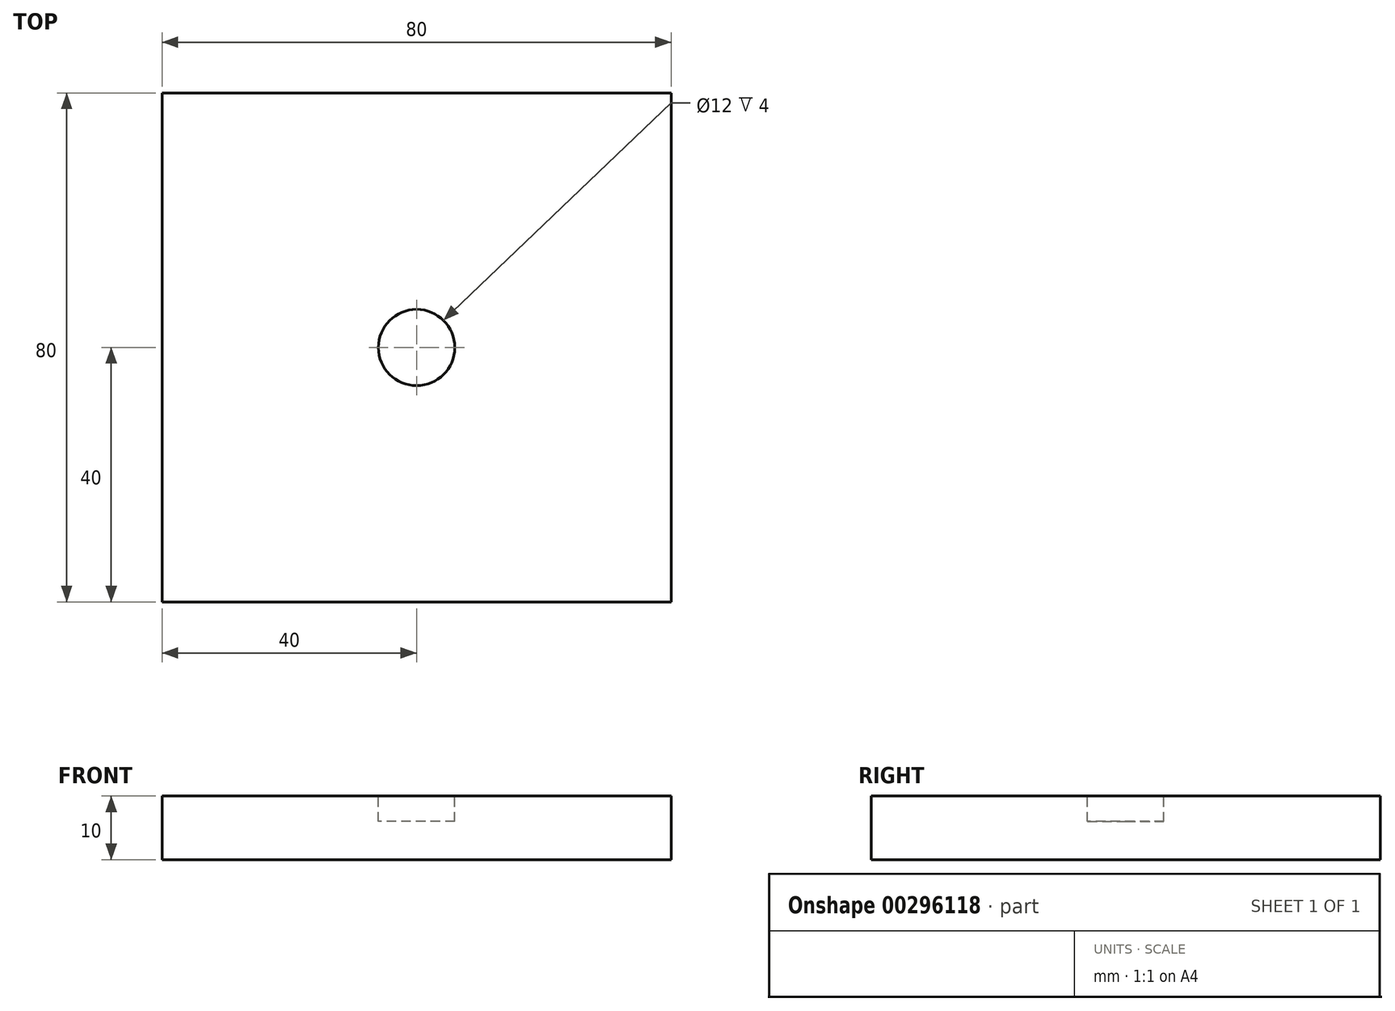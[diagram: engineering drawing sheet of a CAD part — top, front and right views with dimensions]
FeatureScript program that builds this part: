
annotation { "Feature Type Name" : "Feature", "Feature Type Description" : "" }
export const myFeature = defineFeature(function(context is Context, id is Id, definition is map)
    precondition{}
    {
        {
            var Q0;
            Q0=qCreatedBy(makeId("Top.planeOp"),FACE);
            var sketch = newSketch(context, id + "F0", { "sketchPlane" : qUnion([Q0])});
            skLineSegment(sketch, "E0.bottom", {"start": v(40, 40) * mm, "end": v(-40, 40) * mm});
            skLineSegment(sketch, "E0.top", {"start": v(40, -40) * mm, "end": v(-40, -40) * mm});
            skLineSegment(sketch, "E0.left", {"start": v(40, 40) * mm, "end": v(40, -40) * mm});
            skLineSegment(sketch, "E0.right", {"start": v(-40, 40) * mm, "end": v(-40, -40) * mm});
            skPoint(sketch, "E0.middle", {"position": v(0, 0) * mm});
            skSolve(sketch);
        }
        {
            var Q0;
            Q0 = qSketchRegion(id + "F0", true);
            extrude(context, id + "F1", {"entities" : qUnion([Q0]), "oppositeDirection" : true, "depth" : 10 * mm, "offsetDistance" : 25 * mm});
        }
        {
            var Q0;
            Q0=makeQuery(id+"F1.opExtrude","CAP_FACE",FACE,{"disambiguationData":[OSD([sQuery(id+"F0.wireOp",EDGE,"E0.bottom"),sQuery(id+"F0.wireOp",EDGE,"E0.top"),sQuery(id+"F0.wireOp",EDGE,"E0.left"),sQuery(id+"F0.wireOp",EDGE,"E0.right")])],"isStart":true});
            var sketch = newSketch(context, id + "F2", { "sketchPlane" : qUnion([Q0])});
            skCircle(sketch, "E1", {"center": v(0, 0) * mm, "radius": 6 * mm});
            skSolve(sketch);
        }
        {
            var Q0;
            Q0 = qSketchRegion(id + "F2", true);
            extrude(context, id + "F3", {"entities" : qUnion([Q0]), "operationType" : NewBodyOperationType.REMOVE, "oppositeDirection" : true, "depth" : 4 * mm, "offsetDistance" : 25 * mm});
        }
    });
